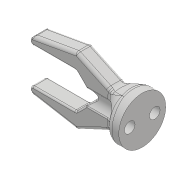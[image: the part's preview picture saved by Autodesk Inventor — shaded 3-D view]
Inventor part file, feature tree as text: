
AUTODESK INVENTOR PART (.ipt)
format: ipt  version: 2018 (Build 220112000, 112)  size: 971,264 bytes
history: native  units: mm
features: fillet x8, sketch x7, projected_geometry x5, extrude x4, plane x3, mirror x1, loft x1, hole x1, other x1
ambient origin geometry x8: Origin, YZ Plane, XZ Plane, XY Plane, X Axis, Y Axis, Z Axis, Center Point
bodies: Solid1 (feature_tree)
feature tree (31):
  extrude  "Extrusion1"  TaperAngle=60.0deg  [1 undecoded]
  mirror  "Mirror1"
  plane  "Work Plane1"
  sketch  "Sketch2"  dims[d2=25.307274mm d3=25.307274mm]
  plane  "Work Plane2"
  extrude  "Extrusion2"  Depth=25.307274mm
  loft  "Loft1"
  extrude  "Extrusion3"  Depth=7.0mm
  fillet  "Fillet1"  Radius=11.0mm
  fillet  "Fillet2"  Radius=14.0mm
  fillet  "Fillet3"  Radius=16.0mm
  fillet  "Fillet4"  Radius=5.0mm
  fillet  "Fillet5"  Radius=10.0mm
  fillet  "Fillet6"  [1 undecoded]
  hole  "Hole1"  [1 undecoded]
  plane  "Work Plane3"
  extrude  "Extrusion4"  TaperAngle=0.0deg  [1 undecoded]
  fillet  "Fillet7"  Radius=3.0mm
  fillet  "Fillet8"  Radius=2.0mm
  sketch  "Sketch1"  dims[d0=8.0mm d1=60.0deg]
  sketch  "Sketch3"  dims[d4=135.0deg d5=135.0deg]
  sketch  "Sketch4"  dims[d6=8.0mm d7=7.0mm d8=11.0mm d9=14.0mm d10=16.0mm d11=5.0mm d12=0.0mm d13=10.0mm d14=-5.0mm]
  projected_geometry  "Projected Loop1"
  other  "Edges1"
  sketch  "Sketch5"  dims[d15=5.0mm d16=0.0mm d17=15.0mm]
  projected_geometry  "Projected Loop2"
  sketch  "Sketch6"  dims[d18=0.0mm d19=90.0deg d20=0.0mm d21=90.0deg d22=3.0mm d23=0.0mm d24=2.0mm]
  projected_geometry  "Projected Loop3"
  sketch  "Sketch7"  dims[d25=2.0mm d26=2.0mm d27=1.0mm d28=1.0mm d29=0.5mm d30=8.0mm d31=3.4mm d32=6.0mm d33=6.3mm d34=2.0mm d35=90.0deg d36=8.0mm d37=20.594885mm d38=-5.0mm d39=6.0mm d40=6.0mm d41=14.0mm d42=0.0mm d43=0.5mm d44=0.5mm]
  projected_geometry  "Projected Loop4"
  projected_geometry  "Project Cut Edges1"
note: 4 required parameter values undecoded (feature->parameter linkage not recoverable at this tier; creation-order binding heuristic only, values carry confidence <= 0.55)
